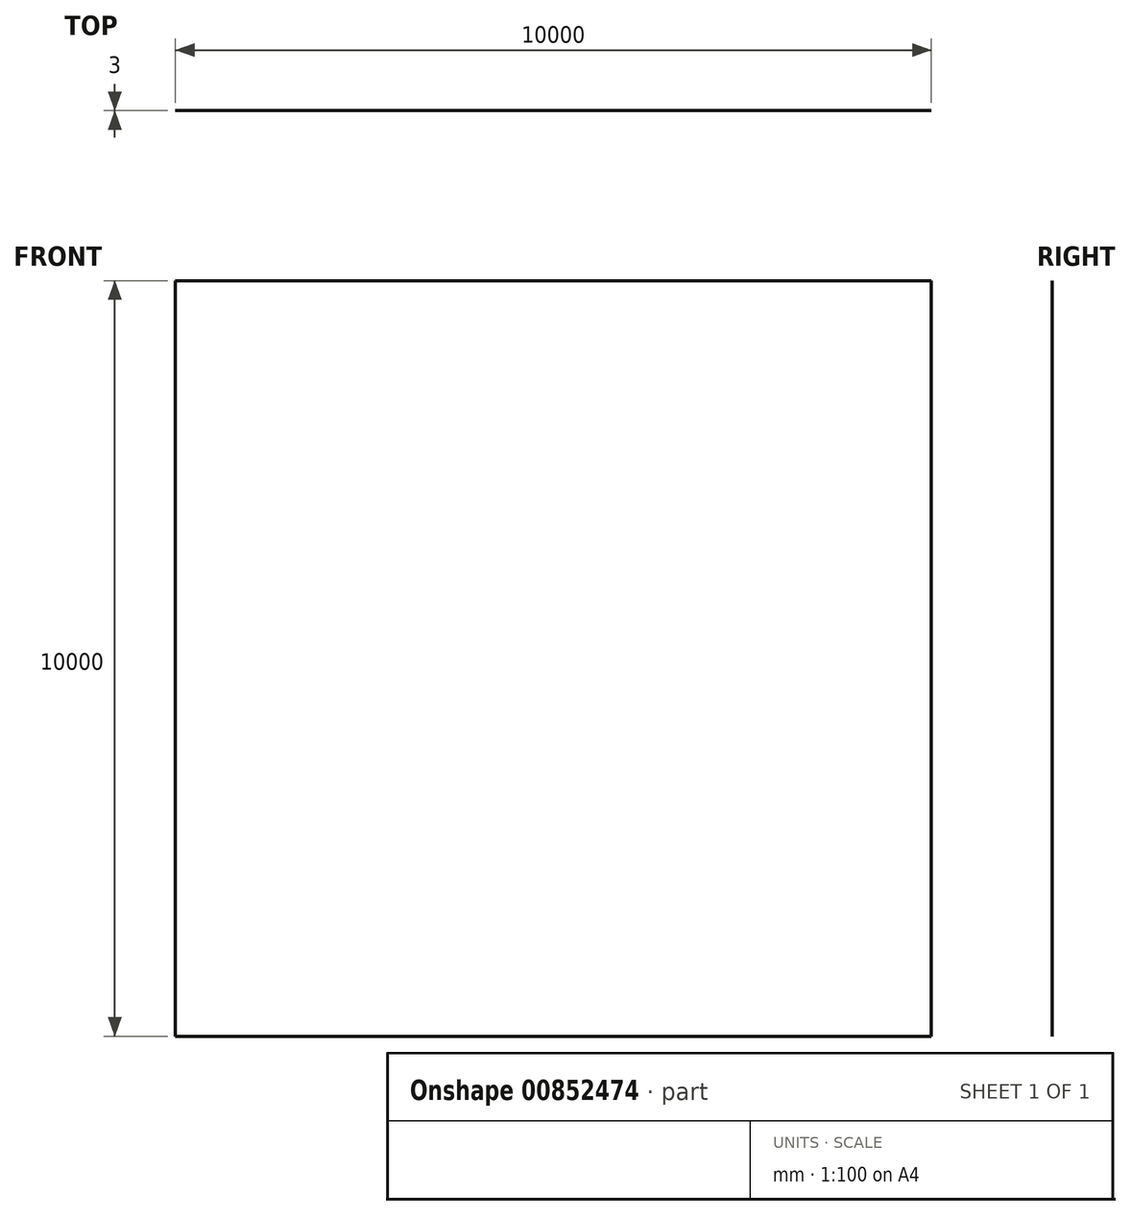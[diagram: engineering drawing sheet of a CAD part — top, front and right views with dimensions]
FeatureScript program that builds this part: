
annotation { "Feature Type Name" : "Feature", "Feature Type Description" : "" }
export const myFeature = defineFeature(function(context is Context, id is Id, definition is map)
    precondition{}
    {
        {
            var Q0;
            Q0=qCreatedBy(makeId("Front.planeOp"),FACE);
            var sketch = newSketch(context, id + "F0", { "sketchPlane" : qUnion([Q0])});
            skLineSegment(sketch, "E0.bottom", {"start": v(5000, -5000) * mm, "end": v(-5000, -5000) * mm});
            skLineSegment(sketch, "E0.top", {"start": v(5000, 5000) * mm, "end": v(-5000, 5000) * mm});
            skLineSegment(sketch, "E0.left", {"start": v(5000, -5000) * mm, "end": v(5000, 5000) * mm});
            skLineSegment(sketch, "E0.right", {"start": v(-5000, -5000) * mm, "end": v(-5000, 5000) * mm});
            skPoint(sketch, "E0.middle", {"position": v(0, 0) * mm});
            skSolve(sketch);
        }
        {
            var Q0;
            Q0 = qSketchRegion(id + "F0", true);
            extrude(context, id + "F1", {"entities" : qUnion([Q0]), "depth" : 3 * mm, "offsetDistance" : 25 * mm});
        }
    });
